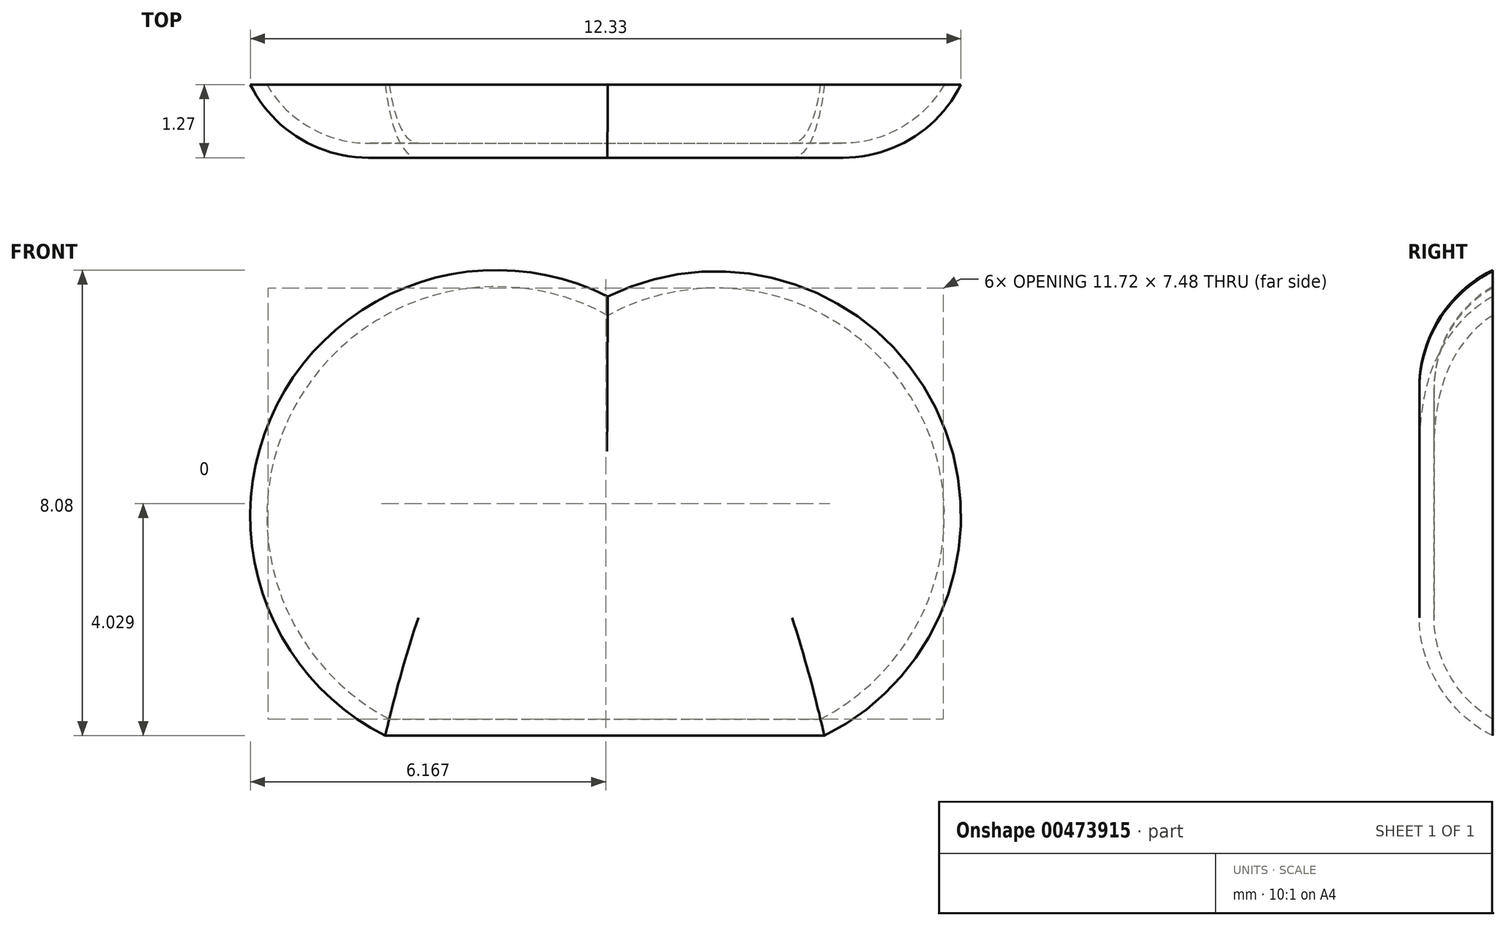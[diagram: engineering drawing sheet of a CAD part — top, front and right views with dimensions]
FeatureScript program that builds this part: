
annotation { "Feature Type Name" : "Feature", "Feature Type Description" : "" }
export const myFeature = defineFeature(function(context is Context, id is Id, definition is map)
    precondition{}
    {
        {
            var Q0;
            Q0=qCreatedBy(makeId("Front.planeOp"),FACE);
            var sketch = newSketch(context, id + "F0", { "sketchPlane" : qUnion([Q0])});
            skLineSegment(sketch, "E0", {"start": v(0, 0) * mm, "end": v(7.62, 0) * mm});
            skArc(sketch, "E1", {"start": v(7.62, 0) * mm, "mid": v(9.55, 5.69) * mm, "end": v(3.86, 7.62) * mm});
            skArc(sketch, "E2", {"start": v(3.86, 7.62) * mm, "mid": v(-1.88, 5.74) * mm, "end": v(0, 0) * mm});
            skSolve(sketch);
        }
        {
            var Q0;
            Q0=makeQuery(id+"F0.imprint","IMPRINT",FACE,{"disambiguationData":[TD([[makeQuery(id+"F0.imprint","IMPRINT",EDGE,{"derivedFrom":sQuery(id+"F0.wireOp",EDGE,"E0")}),1.0]])]});
            extrude(context, id + "F1", {"entities" : qUnion([Q0]), "depth" : 1.27 * mm});
        }
        {
            var Q0;
            Q0=makeQuery(id+"F1.opExtrude","CAP_FACE",FACE,{"disambiguationData":[OSD([sQuery(id+"F0.wireOp",EDGE,"E0"),sQuery(id+"F0.wireOp",EDGE,"E1"),sQuery(id+"F0.wireOp",EDGE,"E2")])],"isStart":false});
            fillet(context, id + "F2", {"entities" : qUnion([Q0]), "radius" : 2.3 * mm, "tangentPropagation" : true, "allowEdgeOverflow" : false});
        }
        {
            var Q0;
            Q0=makeQuery(id+"F1.opExtrude","CAP_FACE",FACE,{"disambiguationData":[OSD([sQuery(id+"F0.wireOp",EDGE,"E0"),sQuery(id+"F0.wireOp",EDGE,"vcwloe8j-naiA-vdPA-0SPQ-ts5Rwr7FJmbM")])],"isStart":true});
            shell(context, id + "F3", {"entities" : qUnion([Q0]), "thickness" : 0.25 * mm});
        }
    });
